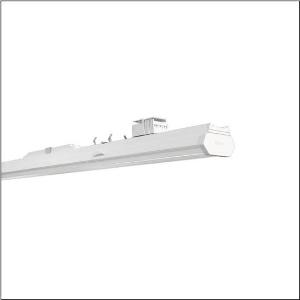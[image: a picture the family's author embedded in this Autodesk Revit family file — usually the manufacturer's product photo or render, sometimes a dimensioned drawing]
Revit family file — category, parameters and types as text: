
# Revit family: licross_11_protected_extreme_ho_51tp12dn6e5me
name_source: partatom
category: Lighting Fixtures
units: mm (PartAtom-declared; Revit-internal decimal feet)

## family parameters
Cut with Voids When Loaded = No
Host = Face
Light Source = No
Part Type = Normal
Room Calculation Point = No
Round Connector Dimension = Use Diameter
Shared = No

## types (1)
- --- (1 x LED, 14910 lm, 87.3 W, 6500K)
    Apparent Load = 87 VA
    CIE Flux Codes = 70 91 97 98 100
    Color Rendering = 80
    Color Temperature = 6500K
    Default Elevation = 1800 mm
    Description = Licross 11 Protected extreme HO, luminaire insert, of sheet steel, galvanised, coil coated, white, length: 1.500mm, width: 90mm, height: 101mm, LED rated luminous flux: 14.910lm, light colour: 865, SDCM (Standard Deviation of Colour Matching)MacAdam ≤ 2 SDCM (initial), control gear: DALI 2, with plug, 5-pole, with phase selection, mains connection: 220..240V, AC, 50/60Hz, rated input power: 87W, internal wiring halogen-free, primary optical cover: cover, of PMMA, light emission: direct distribution, primary light characteristic: symmetric, protection rating (complete): IP64, insulation class (complete): insulation class I (protective earthing), certification: CE, ENEC, VDE, UKCA, protection symbol: D if used in an environment with conductive dust loads with corresponding accessories, impact resistance: IK06, permissible ambient temperature for indoor applications: -40..+40°C, LABS conformity tested according to VDMA 24364:2018-05, reducing of maximum allowable ambient temperature of 5°C with ceiling mounting, corresponds to IFS (International Featured Standards) requirements for safety and quality in the food industry, The light source and the operating device comply with the requirements of the Ecodesign Regulation (EU) 2019/2020 and are replaceable in accordance with this regulation, packaging unit: 1 piece
    Height = 92 mm
    Lamp = 1 x LED
    Lamp Light Flux = 14910 lm
    Lamp Power = 87.3 W
    Lamp count = 1
    Length = 1500 mm
    Luminous efficacy = 171 lm/W
    Manufacturer = Siteco
    ModVariant = No
    Model = 51TP12DN6E5ME
    Mounting Place = Ceiling
    Mounting Type = Pendant
    Number of Poles = 1
    OnlyDefault = Yes
    Power Factor = 1
    Product Name = Licross 11 Protected extreme HO
    Product group = luminaire insert | ceiling pendant
    ProductGroupID = 901
    Protection Class = Protection class I
    Protection Degree = IP 64
    RLX_Detail_Level = 1
    RLX_Emergency_Light_Flux = 0 lm
    RLX_Emergency_Type = 0
    RLX_Emergency_Type_DB = No
    RlxData = <blob elided: 24705 chars, md5=08db1b4a>
    Socket = socket
    Standby Power = 0 W
    System Light Flux = 14910 lm
    System Power = 87 W
    Type Comments = factory setting: luminous flux: 100 % | dim-lin: 254 | 589 mA
    Type Image = l_1256148.jpg
    URL = http://relux.com
    VarID = @adj_031717
    Voltage = 0 V
    Weight = 0.00 kg
    Width = 88 mm

## geometry (parser evidence)
native form markers: Blend x4, Sweep x10
no freeform markers — native parametric forms only
